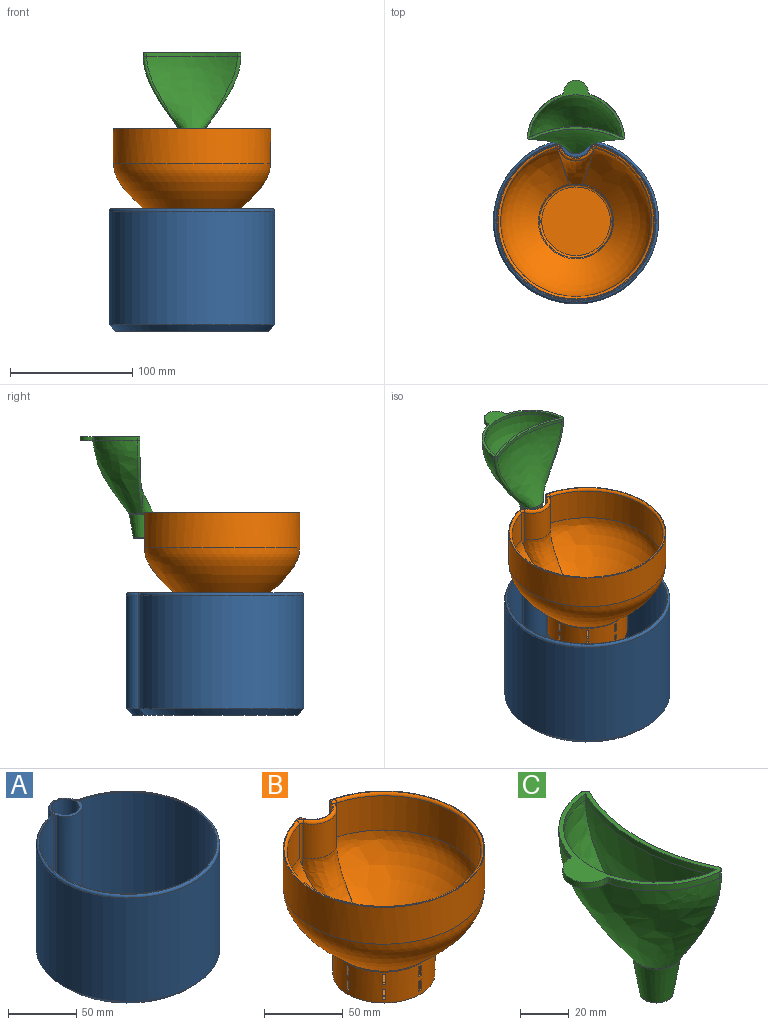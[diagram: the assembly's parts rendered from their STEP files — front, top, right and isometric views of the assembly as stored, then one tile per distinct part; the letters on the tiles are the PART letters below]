
ASSEMBLY  parts=3 mates=2
PART A: 26 faces, bbox 146.1x151.6x100 mm
  f0: cylinder r=10mm len=87mm, axis (0,0,-1), area 5417.8mm2, adj f5,f8,f9,f11,f16,f25
  f1: cylinder r=12.5mm len=92mm, axis (0,0,-1), area 2992.7mm2, adj f5,f8,f13,f23,f24
  f2: cylinder r=12.5mm len=93mm, axis (0,0,-1), area 3161.3mm2, adj f14,f17,f19,f22
  f3: cylinder r=65mm len=130mm, axis (0,0,-1), area 34883.7mm2, adj f5,f12,f23,f24
  f4: cylinder r=67.5mm len=135mm, axis (0,0,-1), area 36863.4mm2, adj f15,f17,f18,f19
  f5: plane 141x131mm, normal (0,0,1), area 299.6mm2, adj f0,f1,f3,f18,f20,f21,f22,f23
  f6: plane 135x125mm, normal (0,0,-1), area 12398.8mm2, adj f14,f15
  f7: plane 120x117.84mm, normal (0,0,1), area 11026mm2, adj f12,f13
  f8: cylinder r=5mm len=13.88mm, axis (0,1,0), area 199.4mm2, adj f0,f1,f13,f25
  f9: plane 14.14x3mm, normal (0,1,0), area 20.4mm2, adj f0,f10,f11,f16
  f10: plane 7.48x0.93mm, normal (0,0,-1), area 4.7mm2, adj f9,f16
  f11: plane 14.14x2.93mm, normal (0,0,1), area 28.5mm2, adj f0,f9
  f12: cone r=60mm half-angle=45deg, axis (0,0,1), area 2571.4mm2, adj f3,f7,f13,f23,f24
  f13: cone r=12.5mm half-angle=45deg, axis (0,0,-1), area 222.6mm2, adj f1,f7,f8,f12,f23,f24
  f14: cone r=12.5mm half-angle=45deg, axis (0,0,1), area 233.8mm2, adj f2,f6,f15,f17,f19
  f15: cone r=67.5mm half-angle=45deg, axis (0,0,1), area 2748.3mm2, adj f4,f6,f14,f17,f19
  f16: cone r=10mm half-angle=45deg, axis (0,0,-1), area 33.7mm2, adj f0,f9,f10
  f17: cylinder r=2mm len=93mm, axis (0,0,1), area 214.3mm2, adj f2,f4,f14,f15,f20
  f18: torus R=65.5mm, axis (0,0,1), area 1231.9mm2, adj f4,f5,f20,f21
  f19: cylinder r=2mm len=93mm, axis (0,0,1), area 214.3mm2, adj f2,f4,f14,f15,f21
  f20: torus R=4mm, axis (0,0,1), area 9.9mm2, adj f5,f17,f18,f22
  f21: torus R=4mm, axis (0,0,1), area 9.9mm2, adj f5,f18,f19,f22
  f22: torus R=10.5mm, axis (0,0,1), area 100.6mm2, adj f2,f5,f20,f21
  f23: cylinder r=2mm len=92.6mm, axis (0,0,-1), area 285.3mm2, adj f1,f3,f5,f12,f13
  f24: cylinder r=2mm len=92.6mm, axis (0,0,-1), area 285.3mm2, adj f1,f3,f5,f12,f13
  f25: sphere r=10mm, area 527mm2, adj f0,f8
PART B: 90 faces, bbox 146x143.3x101.9 mm
  f0: plane 3.18x3.18mm, normal (0,0,1), area 5mm2, adj f1,f3,f56,f57
  f1: plane 7.71x1.77mm, normal (-0.71,-0.71,0), area 19.3mm2, adj f0,f2,f56,f57
  f2: plane 3.18x3.18mm, normal (0,0,-1), area 5mm2, adj f1,f3,f56,f57
  f3: plane 7.71x1.77mm, normal (0.71,0.71,0), area 19.3mm2, adj f0,f2,f56,f57
  f4: plane 3.66x3.66mm, normal (0,0,1), area 6.4mm2, adj f5,f7,f56,f77
  f5: plane 7.73x2.26mm, normal (-0.71,-0.71,0), area 19.6mm2, adj f4,f6,f56,f57,f77
  f6: plane 3.18x3.18mm, normal (0,0,-1), area 5mm2, adj f5,f7,f56,f57
  f7: plane 7.73x2.26mm, normal (0.71,0.71,0), area 19.6mm2, adj f4,f6,f56,f57,f77
  f8: plane 2.52x2mm, normal (0,0,1), area 5mm2, adj f9,f11,f56,f57
  f9: plane 7.71x2.5mm, normal (-1,0,0), area 19.3mm2, adj f8,f10,f56,f57
  f10: plane 2.52x2mm, normal (0,0,-1), area 5mm2, adj f9,f11,f56,f57
  f11: plane 7.71x2.5mm, normal (1,0,0), area 19.3mm2, adj f8,f10,f56,f57
  f12: plane 3.19x2mm, normal (0,0,1), area 6.4mm2, adj f13,f15,f56,f77
  f13: plane 7.73x3.19mm, normal (-1,0,0), area 19.6mm2, adj f12,f14,f56,f57,f77
  f14: plane 2.52x2mm, normal (0,0,-1), area 5mm2, adj f13,f15,f56,f57
  f15: plane 7.73x3.19mm, normal (1,0,0), area 19.6mm2, adj f12,f14,f56,f57,f77
  f16: plane 3.18x3.18mm, normal (0,0,1), area 5mm2, adj f17,f19,f56,f57
  f17: plane 7.71x1.77mm, normal (-0.71,0.71,0), area 19.3mm2, adj f16,f18,f56,f57
  f18: plane 3.18x3.18mm, normal (0,0,-1), area 5mm2, adj f17,f19,f56,f57
  f19: plane 7.71x1.77mm, normal (0.71,-0.71,0), area 19.3mm2, adj f16,f18,f56,f57
  f20: plane 3.66x3.66mm, normal (0,0,1), area 6.4mm2, adj f21,f23,f56,f77
  f21: plane 7.73x2.26mm, normal (-0.71,0.71,0), area 19.6mm2, adj f20,f22,f56,f57,f77
  f22: plane 3.18x3.18mm, normal (0,0,-1), area 5mm2, adj f21,f23,f56,f57
  f23: plane 7.73x2.26mm, normal (0.71,-0.71,0), area 19.6mm2, adj f20,f22,f56,f57,f77
  f24: plane 2.52x2mm, normal (0,0,1), area 5mm2, adj f25,f27,f56,f57
  f25: plane 7.71x2.5mm, normal (0,1,0), area 19.3mm2, adj f24,f26,f56,f57
  f26: plane 2.52x2mm, normal (0,0,-1), area 5mm2, adj f25,f27,f56,f57
  f27: plane 7.71x2.5mm, normal (0,-1,0), area 19.3mm2, adj f24,f26,f56,f57
  f28: plane 3.19x2mm, normal (0,0,1), area 6.4mm2, adj f29,f31,f56,f77
  f29: plane 7.73x3.19mm, normal (0,1,0), area 19.6mm2, adj f28,f30,f56,f57,f77
  f30: plane 2.52x2mm, normal (0,0,-1), area 5mm2, adj f29,f31,f56,f57
  f31: plane 7.73x3.19mm, normal (0,-1,0), area 19.6mm2, adj f28,f30,f56,f57,f77
  f32: plane 3.18x3.18mm, normal (0,0,1), area 5mm2, adj f33,f35,f56,f57
  f33: plane 7.71x1.77mm, normal (0.71,0.71,0), area 19.3mm2, adj f32,f34,f56,f57
  f34: plane 3.18x3.18mm, normal (0,0,-1), area 5mm2, adj f33,f35,f56,f57
  f35: plane 7.71x1.77mm, normal (-0.71,-0.71,0), area 19.3mm2, adj f32,f34,f56,f57
  f36: plane 3.66x3.66mm, normal (0,0,1), area 6.4mm2, adj f37,f39,f56,f77
  f37: plane 7.73x2.26mm, normal (0.71,0.71,0), area 19.6mm2, adj f36,f38,f56,f57,f77
  f38: plane 3.18x3.18mm, normal (0,0,-1), area 5mm2, adj f37,f39,f56,f57
  f39: plane 7.73x2.26mm, normal (-0.71,-0.71,0), area 19.6mm2, adj f36,f38,f56,f57,f77
  f40: plane 2.52x2mm, normal (0,0,1), area 5mm2, adj f41,f43,f56,f57
  f41: plane 7.71x2.5mm, normal (1,0,0), area 19.3mm2, adj f40,f42,f56,f57
  f42: plane 2.52x2mm, normal (0,0,-1), area 5mm2, adj f41,f43,f56,f57
  f43: plane 7.71x2.5mm, normal (-1,0,0), area 19.3mm2, adj f40,f42,f56,f57
  f44: plane 3.19x2mm, normal (0,0,1), area 6.4mm2, adj f45,f47,f56,f77
  f45: plane 7.73x3.19mm, normal (1,0,0), area 19.6mm2, adj f44,f46,f56,f57,f77
  f46: plane 2.52x2mm, normal (0,0,-1), area 5mm2, adj f45,f47,f56,f57
  f47: plane 7.73x3.19mm, normal (-1,0,0), area 19.6mm2, adj f44,f46,f56,f57,f77
  f48: plane 3.18x3.18mm, normal (0,0,1), area 5mm2, adj f49,f51,f56,f57
  f49: plane 7.71x1.77mm, normal (0.71,-0.71,0), area 19.3mm2, adj f48,f50,f56,f57
  f50: plane 3.18x3.18mm, normal (0,0,-1), area 5mm2, adj f49,f51,f56,f57
  f51: plane 7.71x1.77mm, normal (-0.71,0.71,0), area 19.3mm2, adj f48,f50,f56,f57
  f52: plane 3.66x3.66mm, normal (0,0,1), area 6.4mm2, adj f53,f55,f56,f77
  f53: plane 7.73x2.26mm, normal (0.71,-0.71,0), area 19.6mm2, adj f52,f54,f56,f57,f77
  f54: plane 3.18x3.18mm, normal (0,0,-1), area 5mm2, adj f53,f55,f56,f57
  f55: plane 7.73x2.26mm, normal (-0.71,0.71,0), area 19.6mm2, adj f52,f54,f56,f57,f77
  f56: cylinder r=32.5mm len=65mm, axis (0,0,1), area 4675mm2, adj f0,f1,f2,f3,f4,f5,f6,f7
  f57: cylinder r=30mm len=60mm, axis (0,0,1), area 3683.5mm2, adj f0,f1,f2,f3,f5,f6,f7,f8
  f58: plane 65x65mm, normal (0,0,-1), area 3318.3mm2, adj f56
  f59: bspline ~128.62x127.82mm, area 16411.3mm2, adj f60,f63,f83,f84,f85
  f60: bspline ~43.23x31.38mm, area 1232.3mm2, adj f59,f62,f82,f84,f85
  f61: plane 128.4x126.66mm, normal (0,0,1), area 210mm2, adj f62,f63,f84,f85,f86,f87,f88,f89
  f62: cylinder r=13.3mm len=28.67mm, axis (0,0,-1), area 968mm2, adj f60,f61,f84,f85
  f63: cylinder r=64.2mm len=128.4mm, axis (0,0,1), area 10690.8mm2, adj f59,f61,f84,f85
  f64: plane 56x56mm, normal (0,0,1), area 2463mm2, adj f77
  f65: offset ~133.62x132.81mm, area 15120.8mm2, adj f66,f68,f78,f79,f80,f81
  f66: offset ~49.24x37.49mm, area 1249.2mm2, adj f65,f67,f78,f80,f81
  f67: cylinder r=15.8mm len=28.64mm, axis (0,0,-1), area 956.1mm2, adj f66,f80,f81,f87
  f68: cylinder r=61.7mm len=123.4mm, axis (0,0,1), area 9437.5mm2, adj f65,f80,f81,f88
  f69: plane 2.52x2mm, normal (0,0,1), area 5mm2, adj f56,f57,f70,f72
  f70: plane 7.71x2.5mm, normal (0,-1,0), area 19.3mm2, adj f56,f57,f69,f71
  f71: plane 2.52x2mm, normal (0,0,-1), area 5mm2, adj f56,f57,f70,f72
  f72: plane 7.71x2.5mm, normal (0,1,0), area 19.3mm2, adj f56,f57,f69,f71
  f73: plane 3.19x2mm, normal (0,0,1), area 6.4mm2, adj f56,f74,f76,f77
  f74: plane 7.73x3.19mm, normal (0,-1,0), area 19.6mm2, adj f56,f57,f73,f75,f77
  f75: plane 2.52x2mm, normal (0,0,-1), area 5mm2, adj f56,f57,f74,f76
  f76: plane 7.73x3.19mm, normal (0,1,0), area 19.6mm2, adj f56,f57,f73,f75,f77
  f77: torus R=28mm, axis (0,0,1), area 550.6mm2, adj f4,f5,f7,f12,f13,f15,f20,f21
  f78: bspline ~12.86x1.6mm, area 16.1mm2, adj f57,f65,f66,f79
  f79: bspline ~61.37x60.9mm, area 302.8mm2, adj f57,f65,f78
  f80: cylinder r=2mm len=33.02mm, axis (0,0,1), area 84mm2, adj f65,f66,f67,f68,f89
  f81: cylinder r=2mm len=33.02mm, axis (0,0,1), area 84mm2, adj f65,f66,f67,f68,f86
  f82: bspline ~14.18x1.54mm, area 17.3mm2, adj f56,f60,f83
  f83: bspline ~66.38x65.89mm, area 327.7mm2, adj f56,f59,f82
  f84: cylinder r=2mm len=37.16mm, axis (0,0,-1), area 98.4mm2, adj f59,f60,f61,f62,f63
  f85: cylinder r=2mm len=37.16mm, axis (0,0,-1), area 98.4mm2, adj f59,f60,f61,f62,f63
  f86: torus R=4mm, axis (0,0,1), area 12.1mm2, adj f61,f81,f87,f88
  f87: torus R=13.8mm, axis (0,0,1), area 107.5mm2, adj f61,f67,f86,f89
  f88: torus R=63.7mm, axis (0,0,1), area 1124.9mm2, adj f61,f68,f86,f89
  f89: torus R=4mm, axis (0,0,1), area 12.1mm2, adj f61,f80,f87,f88
PART C: 29 faces, bbox 64.3x85.5x87 mm
  f0: cylinder r=40mm len=34.82mm, axis (0,0,-1), area 143.2mm2, adj f2,f6,f15,f26
  f1: cone r=6.67mm half-angle=9.5deg, axis (0,0,1), area 999.1mm2, adj f3,f14,f16,f18,f19,f20,f21,f22
  f2: bspline ~80x60mm, area 5668.7mm2, adj f0,f4,f13,f17,f19,f20,f22,f24
  f3: bspline ~80x60.6mm, area 3369.2mm2, adj f1,f5,f16,f17,f21,f24,f28
  f4: cylinder r=40mm len=34.82mm, axis (0,0,-1), area 143.2mm2, adj f2,f6,f25,f27
  f5: cylinder r=85mm len=73.97mm, axis (0,0,-1), area 229.6mm2, adj f3,f6,f15,f25
  f6: plane 79.71x48.67mm, normal (0,0,1), area 561mm2, adj f0,f4,f5,f10,f11,f12,f15,f25
  f7: cone r=4.69mm half-angle=9.5deg, axis (0,0,1), area 793.4mm2, adj f8,f9,f14
  f8: offset ~84x64.76mm, area 5214.6mm2, adj f7,f9,f10
  f9: offset ~85.47x64.6mm, area 3373.3mm2, adj f7,f8,f11
  f10: cylinder r=38mm len=75.71mm, axis (0,0,-1), area 338.1mm2, adj f6,f8,f11
  f11: cylinder r=87mm len=75.71mm, axis (0,0,-1), area 235mm2, adj f6,f9,f10
  f12: cylinder r=10mm len=20mm, axis (0,0,-1), area 93mm2, adj f6,f13,f26,f27
  f13: plane 24.05x12.87mm, normal (0,0,-1), area 166.3mm2, adj f2,f12,f26,f27
  f14: torus R=5.82mm, axis (0,0,1), area 112.8mm2, adj f1,f7
  f15: cylinder r=2mm len=3mm, axis (0,0,1), area 12.6mm2, adj f0,f5,f6,f17
  f16: bspline ~5.68x2.04mm, area 3.4mm2, adj f1,f3,f18
  f17: bspline ~61.22x30.13mm, area 222.5mm2, adj f2,f3,f15,f18
  f18: bspline ~0.88x0.38mm, area 0.1mm2, adj f1,f16,f17,f19
  f19: bspline ~9.58x5.68mm, area 9.9mm2, adj f1,f2,f18,f20
  f20: bspline ~11.71x2.45mm, area 10mm2, adj f1,f2,f19,f22
  f21: bspline ~5.68x2.04mm, area 3.4mm2, adj f1,f3,f23
  f22: bspline ~9.58x5.68mm, area 9.9mm2, adj f1,f2,f20,f23
  f23: bspline ~0.88x0.38mm, area 0.1mm2, adj f1,f21,f22,f24
  f24: bspline ~59.61x29.55mm, area 222.5mm2, adj f2,f3,f23,f25
  f25: cylinder r=2mm len=3mm, axis (0,0,1), area 12.7mm2, adj f4,f5,f6,f24
  f26: cylinder r=2mm len=3mm, axis (0,0,1), area 7.6mm2, adj f0,f6,f12,f13
  f27: cylinder r=2mm len=3mm, axis (0,0,1), area 7.6mm2, adj f4,f6,f12,f13
  f28: bspline ~16.07x4.05mm, area 16.1mm2, adj f1,f3
PLACE A rot(axis=(0,0,-1),0deg) t=(-97.96,14.91,55.44)mm
PLACE B t=(-97.96,14.91,120.74)mm
PLACE C rot(axis=(0,0,-1),90deg) t=(-97.96,79.91,199.72)mm
MATE slider B.f56 <-> A.f3  axis (0,0,1) through (-97.96,14.91,123.84)mm
MATE cylindrical C.f1 <-> A.f0  axis (0,0,1) through (-97.96,79.91,219.72)mm
